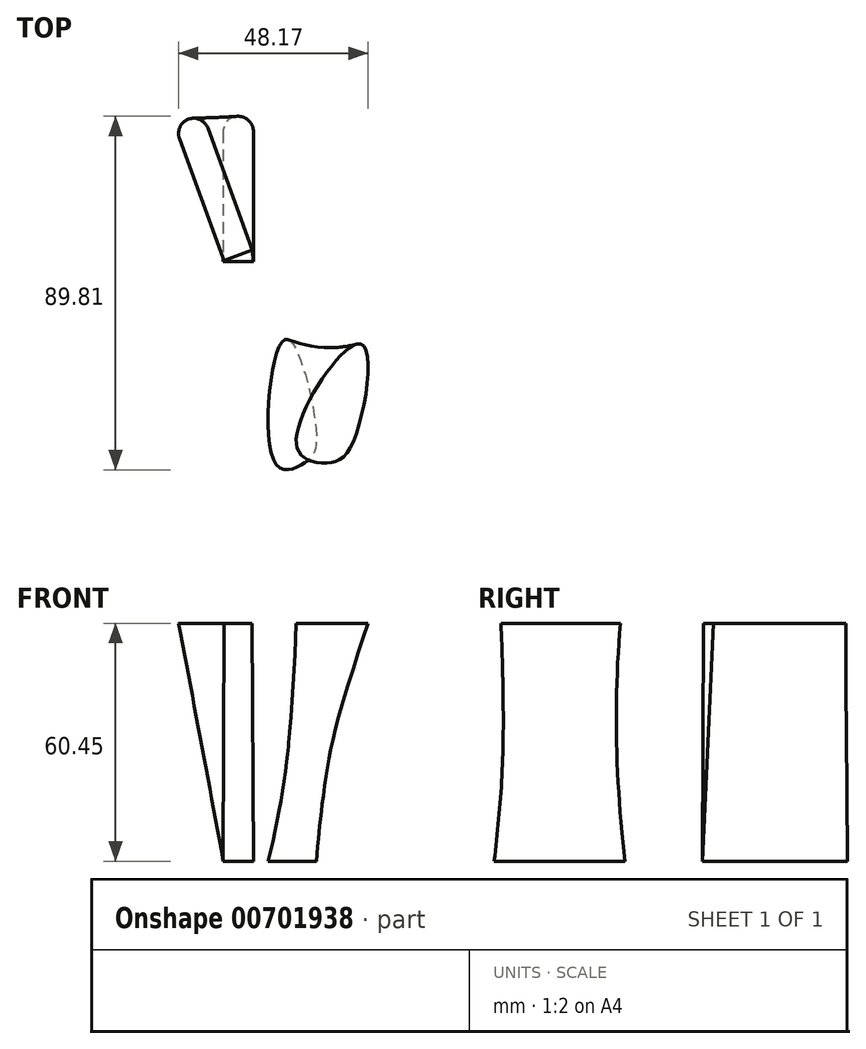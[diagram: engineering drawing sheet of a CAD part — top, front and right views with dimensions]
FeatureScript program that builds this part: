
annotation { "Feature Type Name" : "Feature", "Feature Type Description" : "" }
export const myFeature = defineFeature(function(context is Context, id is Id, definition is map)
    precondition{}
    {
        {
            var Q0;
            Q0=qCreatedBy(makeId("Top.planeOp"),FACE);
            cPlane(context, id + "F0", {"entities" : qUnion([Q0]), "cplaneType" : CPlaneType.OFFSET, "offset" : 60.45 * mm, "width" : 152.4 * mm, "height" : 152.4 * mm});
        }
        {
            var Q0;
            Q0=qCreatedBy(makeId("Top.planeOp"),FACE);
            var sketch = newSketch(context, id + "F1", { "sketchPlane" : qUnion([Q0])});
            skLineSegment(sketch, "E0", {"start": v(0, 33.02) * mm, "end": v(0, 0) * mm});
            skLineSegment(sketch, "E1", {"start": v(0, 0) * mm, "end": v(7.67, 0) * mm});
            skLineSegment(sketch, "E2", {"start": v(7.67, 0) * mm, "end": v(7.67, 33.02) * mm});
            skArc(sketch, "E3", {"start": v(7.67, 33.02) * mm, "mid": v(3.83, 36.86) * mm, "end": v(0, 33.02) * mm});
            skSolve(sketch);
        }
        {
            var Q0;
            Q0=qCreatedBy(id+"F0.planeOp",FACE);
            var sketch = newSketch(context, id + "F2", { "sketchPlane" : qUnion([Q0])});
            skLineSegment(sketch, "E4", {"start": v(-11.11, 31.23) * mm, "end": v(0.18, 0.2) * mm});
            skLineSegment(sketch, "E5", {"start": v(0.18, 0.2) * mm, "end": v(7.4, 2.82) * mm});
            skLineSegment(sketch, "E6", {"start": v(7.4, 2.82) * mm, "end": v(-3.9, 33.85) * mm});
            skArc(sketch, "E7", {"start": v(-3.9, 33.85) * mm, "mid": v(-8.82, 36.14) * mm, "end": v(-11.11, 31.23) * mm});
            skLineSegment(sketch, "E8.0", {"start": v(-11.11, 31.23) * mm, "end": v(-3.9, 33.85) * mm, "construction": true});
            skSolve(sketch);
        }
        {
            var Q0;
            Q0=makeQuery(id+"F1.imprint","IMPRINT",FACE,{"disambiguationData":[TD([[makeQuery(id+"F1.imprint","IMPRINT",EDGE,{"derivedFrom":sQuery(id+"F1.wireOp",EDGE,"E0")}),1.0]])]});
            var Q1;
            Q1=makeQuery(id+"F2.imprint","IMPRINT",FACE,{"disambiguationData":[TD([[makeQuery(id+"F2.imprint","IMPRINT",EDGE,{"derivedFrom":sQuery(id+"F2.wireOp",EDGE,"E4")}),1.0]])]});
            loft(context, id + "F3", {"sheetProfilesArray" : [{ "sheetProfileEntities" : qUnion([Q0]) }, { "sheetProfileEntities" : qUnion([Q1]) }]});
        }
        {
            var Q0;
            Q0=qCreatedBy(makeId("Top.planeOp"),FACE);
            var sketch = newSketch(context, id + "F4", { "sketchPlane" : qUnion([Q0])});
            skFitSpline(sketch, "E9", {"points": [v(20.79, -51.09) * mm, v(13.3, -51.4) * mm, v(15.7, -19.83) * mm, v(23.6, -43.34) * mm, v(20.79, -51.09) * mm]});
            skSolve(sketch);
        }
        {
            var Q0;
            Q0=qCreatedBy(id+"F0.planeOp",FACE);
            var sketch = newSketch(context, id + "F5", { "sketchPlane" : qUnion([Q0])});
            skFitSpline(sketch, "E10", {"points": [v(34.78, -20.93) * mm, v(18.55, -46.02) * mm, v(25.94, -51.25) * mm, v(33.08, -45.67) * mm, v(34.78, -20.93) * mm]});
            skSolve(sketch);
        }
        {
            var Q0;
            Q0=makeQuery(id+"F4.imprint","IMPRINT",FACE,{"disambiguationData":[TD([[makeQuery(id+"F4.imprint","IMPRINT",EDGE,{"derivedFrom":sQuery(id+"F4.wireOp",EDGE,"E9")}),-1.0]])]});
            var Q1;
            Q1=makeQuery(id+"F5.imprint","IMPRINT",FACE,{"disambiguationData":[TD([[makeQuery(id+"F5.imprint","IMPRINT",EDGE,{"derivedFrom":sQuery(id+"F5.wireOp",EDGE,"E10")}),1.0]])]});
            loft(context, id + "F6", {"sheetProfilesArray" : [{ "sheetProfileEntities" : qUnion([Q0]) }, { "sheetProfileEntities" : qUnion([Q1]) }]});
        }
    });
